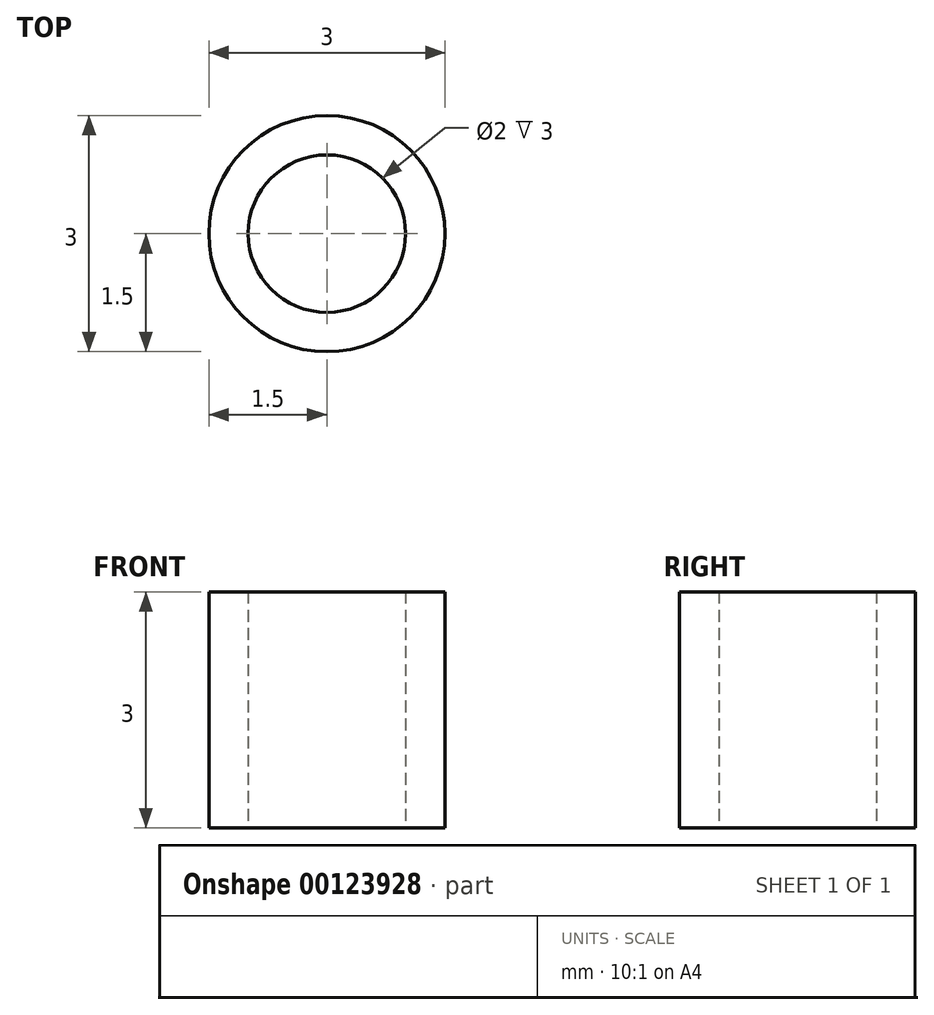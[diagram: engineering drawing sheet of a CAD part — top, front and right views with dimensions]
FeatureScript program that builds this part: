
annotation { "Feature Type Name" : "Feature", "Feature Type Description" : "" }
export const myFeature = defineFeature(function(context is Context, id is Id, definition is map)
    precondition{}
    {
        {
            var Q0;
            Q0=qCreatedBy(makeId("Top.planeOp"),FACE);
            var sketch = newSketch(context, id + "F0", { "sketchPlane" : qUnion([Q0])});
            skCircle(sketch, "E0", {"center": v(0, 0) * mm, "radius": 1.5 * mm});
            skCircle(sketch, "E1", {"center": v(0, 0) * mm, "radius": 1 * mm});
            skSolve(sketch);
        }
        {
            var Q0;
            Q0 = qSketchRegion(id + "F0", true);
            extrude(context, id + "F1", {"entities" : qUnion([Q0]), "depth" : 3 * mm});
        }
    });
